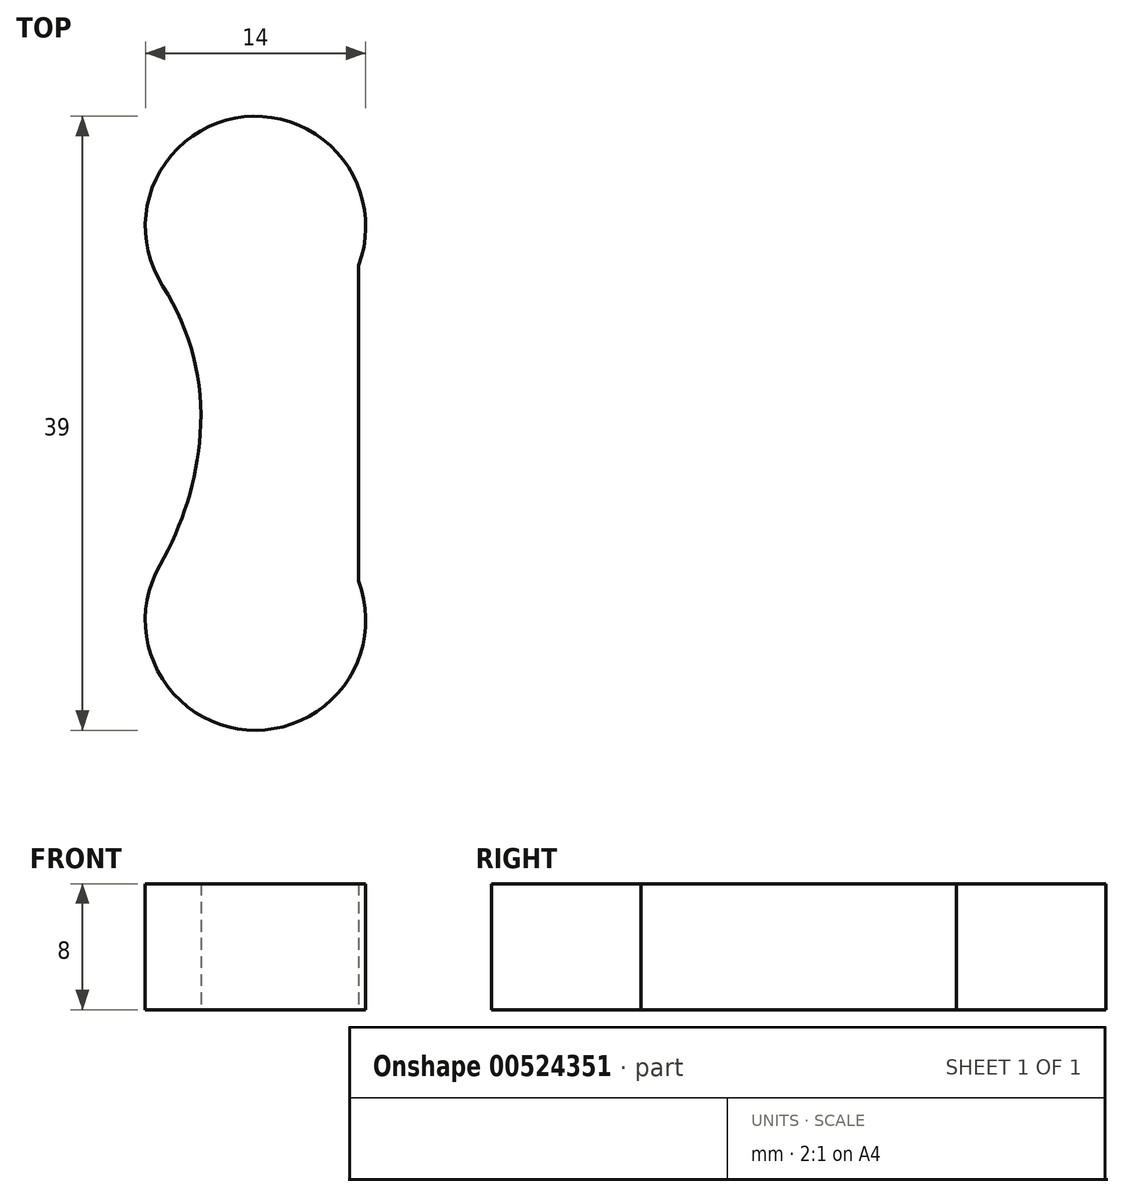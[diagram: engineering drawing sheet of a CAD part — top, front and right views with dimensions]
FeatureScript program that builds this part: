
annotation { "Feature Type Name" : "Feature", "Feature Type Description" : "" }
export const myFeature = defineFeature(function(context is Context, id is Id, definition is map)
    precondition{}
    {
        {
            var Q0;
            Q0=qCreatedBy(makeId("Top.planeOp"),FACE);
            var sketch = newSketch(context, id + "F0", { "sketchPlane" : qUnion([Q0])});
            skCircle(sketch, "E0", {"center": v(-11.13, 34.93) * mm, "radius": 7 * mm});
            skCircle(sketch, "E1", {"center": v(-11.13, 34.93) * mm, "radius": 0.75 * mm});
            skLineSegment(sketch, "E2.bottom", {"start": v(-14.59, 32.83) * mm, "end": v(-4.59, 32.83) * mm});
            skLineSegment(sketch, "E2.top", {"start": v(-14.59, 11.83) * mm, "end": v(-4.59, 11.83) * mm});
            skLineSegment(sketch, "E2.left", {"start": v(-14.59, 32.83) * mm, "end": v(-14.59, 11.83) * mm});
            skLineSegment(sketch, "E2.right", {"start": v(-4.59, 32.83) * mm, "end": v(-4.59, 11.83) * mm});
            skCircle(sketch, "E3.0.1.0", {"center": v(-11.13, 9.93) * mm, "radius": 7 * mm});
            skLineSegment(sketch, "E3.direction2", {"start": v(-11.13, 34.93) * mm, "end": v(-11.13, 9.93) * mm, "construction": true});
            skSolve(sketch);
        }
        {
            var Q0;
            {var subQ0=sQuery(id+"F0.wireOp",EDGE,"E2.top");Q0=makeQuery(id+"F0.imprint","IMPRINT",FACE,{"disambiguationData":[TD([[makeQuery(id+"F0.imprint","IMPRINT",EDGE,{"derivedFrom":subQ0}),-1.0]])]});}
            var Q1;
            {var subQ5=sQuery(id+"F0.wireOp",EDGE,"E2.bottom");Q1=makeQuery(id+"F0.imprint","IMPRINT",FACE,{"disambiguationData":[TD([[makeQuery(id+"F0.imprint","IMPRINT",EDGE,{"derivedFrom":subQ5}),-1.0]])]});}
            var Q2;
            {var subQ0=sQuery(id+"F0.wireOp",EDGE,"E2.left");var subQ1=sQuery(id+"F0.wireOp",EDGE,"E0");var subQ2=makeQuery(id+"F0.imprint","INTERSECT",VERTEX,{"derivedFrom":[subQ1,subQ0]});Q2=makeQuery(id+"F0.imprint","IMPRINT",FACE,{"disambiguationData":[TD([[makeQuery(id+"F0.imprint","IMPRINT",EDGE,{"disambiguationData":[TD([[subQ2,-1.0]])],"derivedFrom":subQ1}),-1.0]])]});}
            var Q3;
            Q3=makeQuery(id+"F0.imprint","IMPRINT",FACE,{"disambiguationData":[TD([[makeQuery(id+"F0.imprint","IMPRINT",EDGE,{"derivedFrom":sQuery(id+"F0.wireOp",EDGE,"E1")}),-1.0]])]});
            var Q4;
            {var subQ0=sQuery(id+"F0.wireOp",EDGE,"E2.top");Q4=makeQuery(id+"F0.imprint","IMPRINT",FACE,{"disambiguationData":[TD([[makeQuery(id+"F0.imprint","IMPRINT",EDGE,{"derivedFrom":subQ0}),1.0]])]});}
            var Q5;
            Q5=makeQuery(id+"F0.imprint","IMPRINT",FACE,{"disambiguationData":[TD([[makeQuery(id+"F0.imprint","IMPRINT",EDGE,{"derivedFrom":sQuery(id+"F0.wireOp",EDGE,"E1")}),1.0]])]});
            extrude(context, id + "F1", {"entities" : qUnion([Q0, Q1, Q2, Q3, Q4, Q5]), "depth" : 8 * mm, "offsetDistance" : 25 * mm});
        }
        {
            var Q0;
            Q0=makeQuery(id+"F1.opExtrude","SWEPT_EDGE",EDGE,{"disambiguationData":[OSD([sQuery(id+"F0.wireOp",EDGE,"E2.left"),sQuery(id+"F0.wireOp",EDGE,"E3.0.1.0")])]});
            fillet(context, id + "F2", {"entities" : qUnion([Q0]), "radius" : 19.71 * mm, "tangentPropagation" : true, "allowEdgeOverflow" : false});
        }
        {
            var Q0;
            Q0=makeQuery(id+"F1.opExtrude","SWEPT_EDGE",EDGE,{"disambiguationData":[OSD([sQuery(id+"F0.wireOp",EDGE,"E0"),sQuery(id+"F0.wireOp",EDGE,"E2.left")])]});
            fillet(context, id + "F3", {"entities" : qUnion([Q0]), "radius" : 15.26 * mm, "tangentPropagation" : true, "allowEdgeOverflow" : false});
        }
    });
